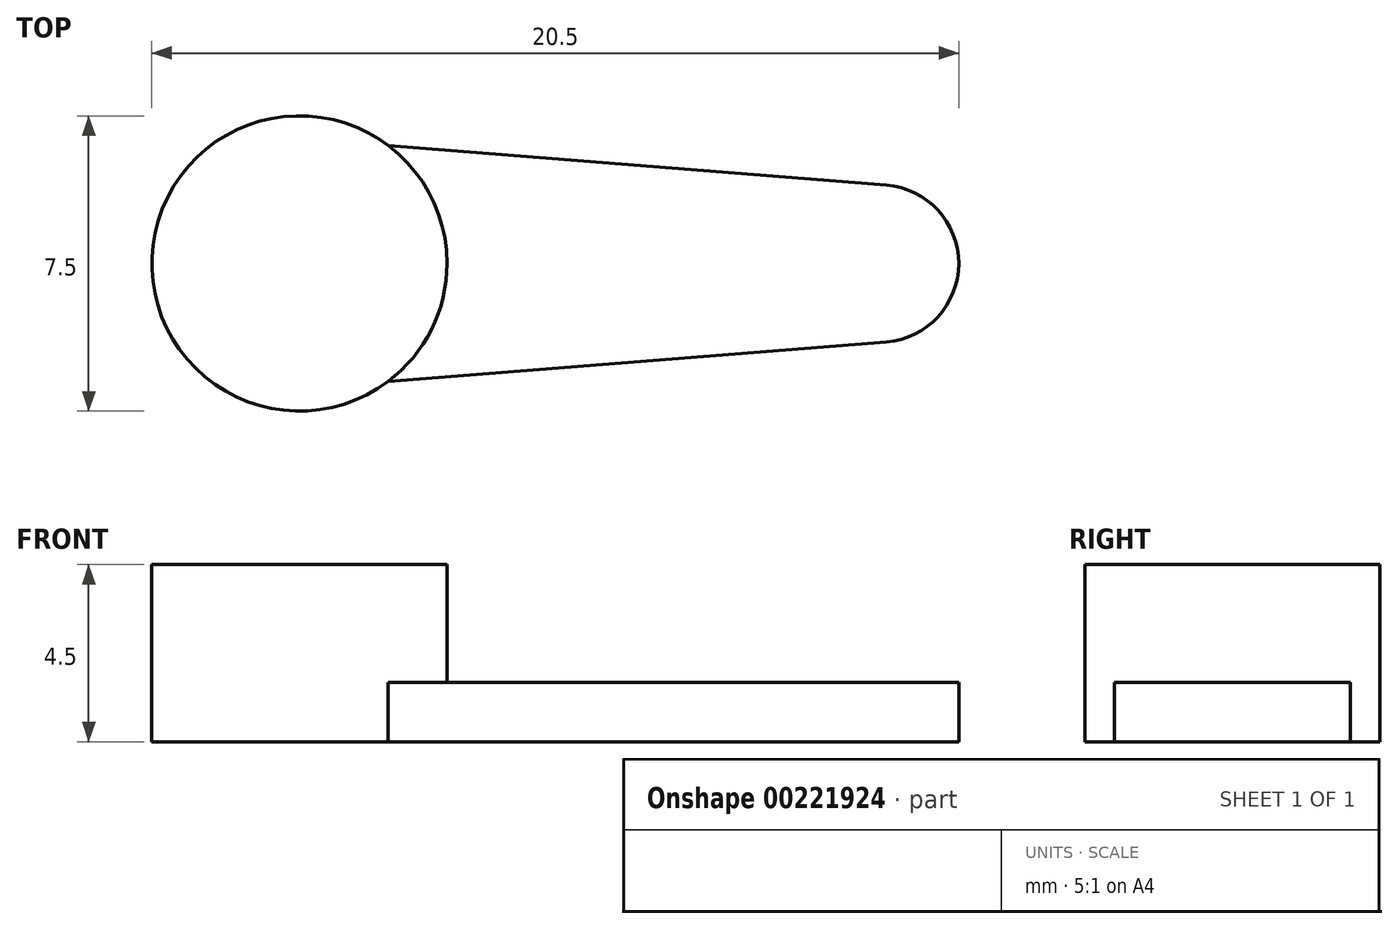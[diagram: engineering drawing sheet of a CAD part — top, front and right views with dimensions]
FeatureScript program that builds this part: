
annotation { "Feature Type Name" : "Feature", "Feature Type Description" : "" }
export const myFeature = defineFeature(function(context is Context, id is Id, definition is map)
    precondition{}
    {
        {
            var Q0;
            Q0=qCreatedBy(makeId("Top.planeOp"),FACE);
            var sketch = newSketch(context, id + "F0", { "sketchPlane" : qUnion([Q0])});
            skCircle(sketch, "E0", {"center": v(0, 0) * mm, "radius": 3.75 * mm});
            skLineSegment(sketch, "E1", {"start": v(0, 0) * mm, "end": v(27.68, 0) * mm, "construction": true});
            skLineSegment(sketch, "E2", {"start": v(2.25, 3) * mm, "end": v(17.53, 1.79) * mm});
            skLineSegment(sketch, "E3.MirrorCS", {"start": v(2.25, -3) * mm, "end": v(17.53, -1.79) * mm});
            skCircle(sketch, "E4", {"center": v(14.75, 0) * mm, "radius": 2 * mm});
            skSolve(sketch);
        }
        {
            var Q0;
            {var subQ0=sQuery(id+"F0.wireOp",EDGE,"E2");var subQ1=sQuery(id+"F0.wireOp",EDGE,"E0");var subQ2=makeQuery(id+"F0.imprint","INTERSECT",VERTEX,{"disambiguationData":[OD(0.0)],"derivedFrom":[subQ1,subQ0]});Q0=makeQuery(id+"F0.imprint","IMPRINT",FACE,{"disambiguationData":[TD([[makeQuery(id+"F0.imprint","IMPRINT",EDGE,{"disambiguationData":[TD([[subQ2,-1.0]])],"derivedFrom":subQ1}),1.0]])]});}
            var Q1;
            {var subQ0=sQuery(id+"F0.wireOp",EDGE,"4a38fa87-aac0-4876-bdf7-fa945dc5d2c0");Q1=makeQuery(id+"F0.imprint","IMPRINT",FACE,{"disambiguationData":[TD([[makeQuery(id+"F0.imprint","IMPRINT",EDGE,{"derivedFrom":subQ0}),-1.0]])]});}
            var Q2;
            {var subQ0=sQuery(id+"F0.wireOp",EDGE,"E4");var subQ1=makeQuery(id+"F0.imprint","INTERSECT",VERTEX,{"derivedFrom":[sQuery(id+"F0.wireOp",EDGE,"E2"),subQ0]});Q2=makeQuery(id+"F0.imprint","IMPRINT",FACE,{"disambiguationData":[TD([[makeQuery(id+"F0.imprint","IMPRINT",EDGE,{"disambiguationData":[TD([[subQ1,-1.0]])],"derivedFrom":subQ0}),1.0]])]});}
            var Q3;
            {var subQ0=sQuery(id+"F0.wireOp",EDGE,"E2");var subQ1=sQuery(id+"F0.wireOp",EDGE,"E0");var subQ2=makeQuery(id+"F0.imprint","INTERSECT",VERTEX,{"derivedFrom":[subQ1,subQ0]});Q3=makeQuery(id+"F0.imprint","IMPRINT",FACE,{"disambiguationData":[TD([[makeQuery(id+"F0.imprint","IMPRINT",EDGE,{"disambiguationData":[TD([[subQ2,1.0]])],"derivedFrom":subQ1}),-1.0]])]});}
            extrude(context, id + "F1", {"entities" : qUnion([Q0, Q1, Q2, Q3]), "depth" : 1.5 * mm});
        }
        {
            var Q0;
            {var subQ0=sQuery(id+"F0.wireOp",EDGE,"E2");var subQ1=sQuery(id+"F0.wireOp",EDGE,"E0");var subQ2=makeQuery(id+"F0.imprint","INTERSECT",VERTEX,{"disambiguationData":[OD(0.0)],"derivedFrom":[subQ1,subQ0]});Q0=makeQuery(id+"F0.imprint","IMPRINT",FACE,{"disambiguationData":[TD([[makeQuery(id+"F0.imprint","IMPRINT",EDGE,{"disambiguationData":[TD([[subQ2,-1.0]])],"derivedFrom":subQ1}),1.0]])]});}
            extrude(context, id + "F2", {"entities" : qUnion([Q0]), "operationType" : NewBodyOperationType.ADD, "depth" : 4.5 * mm});
        }
    });
